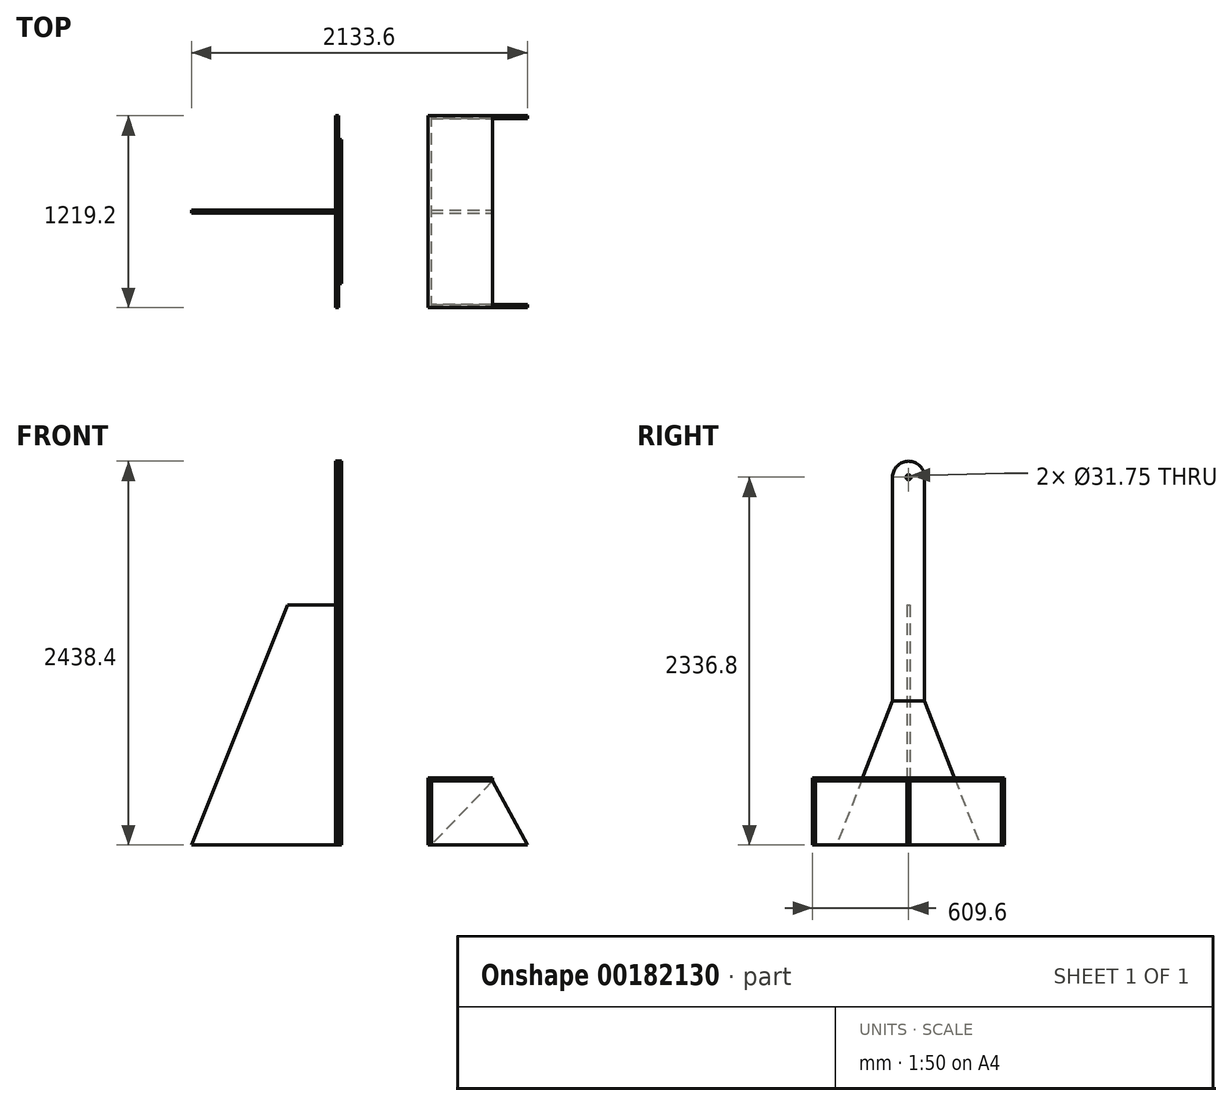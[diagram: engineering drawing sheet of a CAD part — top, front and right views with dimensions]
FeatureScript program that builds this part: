
annotation { "Feature Type Name" : "Feature", "Feature Type Description" : "" }
export const myFeature = defineFeature(function(context is Context, id is Id, definition is map)
    precondition{}
    {
        {
            var Q0;
            Q0=qCreatedBy(makeId("Right.planeOp"),FACE);
            var sketch = newSketch(context, id + "F0", { "sketchPlane" : qUnion([Q0])});
            skLineSegment(sketch, "E0", {"start": v(0, 0) * mm, "end": v(0, 2438.4) * mm, "construction": true});
            skLineSegment(sketch, "E1", {"start": v(-609.6, 0) * mm, "end": v(609.6, 0) * mm, "construction": true});
            skArc(sketch, "E2", {"start": v(101.6, 2336.8) * mm, "mid": v(0, 2438.4) * mm, "end": v(-101.6, 2336.8) * mm});
            skLineSegment(sketch, "E3", {"start": v(-101.6, 2336.8) * mm, "end": v(-101.6, 406.4) * mm});
            skLineSegment(sketch, "E4", {"start": v(101.6, 2336.8) * mm, "end": v(101.6, 406.4) * mm});
            skLineSegment(sketch, "E5", {"start": v(-609.6, 0) * mm, "end": v(-609.6, 406.4) * mm, "construction": true});
            skLineSegment(sketch, "E6", {"start": v(-609.6, 406.4) * mm, "end": v(-101.6, 406.4) * mm, "construction": true});
            skLineSegment(sketch, "E7", {"start": v(101.6, 2336.8) * mm, "end": v(-101.6, 2336.8) * mm, "construction": true});
            skLineSegment(sketch, "E8.MirrorCS", {"start": v(609.6, 406.4) * mm, "end": v(101.6, 406.4) * mm, "construction": true});
            skLineSegment(sketch, "E9.MirrorCS", {"start": v(609.6, 0) * mm, "end": v(609.6, 406.4) * mm, "construction": true});
            skLineSegment(sketch, "E10", {"start": v(-101.6, 406.4) * mm, "end": v(101.6, 406.4) * mm});
            skSolve(sketch);
        }
        {
            var Q0;
            Q0 = qSketchRegion(id + "F0", true);
            var Q1;
            Q1 = qConstructionFilter(qBodyType(qCreatedBy(id + "F0" ,EDGE), BodyType.WIRE), ConstructionObject.NO);
            extrude(context, id + "F1", {"entities" : qUnion([Q0]), "surfaceEntities" : qUnion([Q1]), "depth" : 19.05 * mm});
        }
        {
            var Q0;
            Q0=qCreatedBy(makeId("Right.planeOp"),FACE);
            var sketch = newSketch(context, id + "F2", { "sketchPlane" : qUnion([Q0])});
            skLineSegment(sketch, "E11.0", {"start": v(-609.6, 0) * mm, "end": v(-609.6, 406.4) * mm});
            skLineSegment(sketch, "E12.0", {"start": v(-609.6, 0) * mm, "end": v(609.6, 0) * mm});
            skLineSegment(sketch, "E13.0", {"start": v(609.6, 0) * mm, "end": v(609.6, 406.4) * mm});
            skLineSegment(sketch, "E14", {"start": v(-609.6, 406.4) * mm, "end": v(609.6, 406.4) * mm});
            skSolve(sketch);
        }
        {
            var Q0;
            Q0 = qSketchRegion(id + "F2", true);
            var Q1;
            Q1=makeQuery(id+"F1.opExtrude","CAP_FACE",FACE,{"disambiguationData":[OSD([sQuery(id+"F0.wireOp",EDGE,"E2"),sQuery(id+"F0.wireOp",EDGE,"E3"),sQuery(id+"F0.wireOp",EDGE,"E4"),sQuery(id+"F0.wireOp",EDGE,"E10")])],"isStart":false});
            extrude(context, id + "F3", {"entities" : qUnion([Q0]), "endBound" : BoundingType.UP_TO_SURFACE, "endBoundEntityFace" : qUnion([Q1]), "depth" : 25.4 * mm});
        }
        {
            var Q0;
            Q0=qCreatedBy(makeId("Right.planeOp"),FACE);
            cPlane(context, id + "F4", {"entities" : qUnion([Q0]), "cplaneType" : CPlaneType.OFFSET, "offset" : 304.8 * mm, "width" : 152.4 * mm, "height" : 152.4 * mm});
        }
        {
            var Q0;
            Q0=makeQuery(id+"F3.opExtrude","SWEPT_BODY",BODY,{"disambiguationData":[OSD([sQuery(id+"F2.wireOp",EDGE,"E11.0"),sQuery(id+"F2.wireOp",EDGE,"E12.0"),sQuery(id+"F2.wireOp",EDGE,"E13.0"),sQuery(id+"F2.wireOp",EDGE,"E14")])]});
            var Q1;
            Q1=qCreatedBy(id+"F4.planeOp",FACE);
            mirror(context, id + "F5", {"entities" : qUnion([Q0]), "mirrorPlane" : qUnion([Q1])});
        }
        {
            var Q0;
            Q0=makeQuery(id+"F1.opExtrude","CAP_FACE",FACE,{"disambiguationData":[OSD([sQuery(id+"F0.wireOp",EDGE,"E2"),sQuery(id+"F0.wireOp",EDGE,"E3"),sQuery(id+"F0.wireOp",EDGE,"E4"),sQuery(id+"F0.wireOp",EDGE,"E10")])],"isStart":false});
            var sketch = newSketch(context, id + "F6", { "sketchPlane" : qUnion([Q0])});
            skLineSegment(sketch, "E15", {"start": v(-101.6, 914.4) * mm, "end": v(101.6, 914.4) * mm});
            skLineSegment(sketch, "E16", {"start": v(-457.2, 0) * mm, "end": v(457.2, 0) * mm});
            skLineSegment(sketch, "E17", {"start": v(-101.6, 914.4) * mm, "end": v(-457.2, 0) * mm});
            skLineSegment(sketch, "E18", {"start": v(101.6, 914.4) * mm, "end": v(457.2, 0) * mm});
            skSolve(sketch);
        }
        {
            var Q0;
            Q0 = qSketchRegion(id + "F6", true);
            extrude(context, id + "F7", {"entities" : qUnion([Q0]), "depth" : 19.05 * mm});
        }
        {
            var Q0;
            Q0=makeQuery(id+"F5.opPattern","COPY",FACE,{"derivedFrom":makeQuery(id+"F3.opExtrude","SWEPT_FACE",FACE,{"disambiguationData":[OSD([sQuery(id+"F2.wireOp",EDGE,"E14")])]}),"instanceName":"1"});
            var sketch = newSketch(context, id + "F8", { "sketchPlane" : qUnion([Q0])});
            skLineSegment(sketch, "E19.bottom", {"start": v(590.55, -609.6) * mm, "end": v(996.95, -609.6) * mm});
            skLineSegment(sketch, "E19.top", {"start": v(590.55, 609.6) * mm, "end": v(996.95, 609.6) * mm});
            skLineSegment(sketch, "E19.left", {"start": v(590.55, -609.6) * mm, "end": v(590.55, 609.6) * mm});
            skLineSegment(sketch, "E19.right", {"start": v(996.95, -609.6) * mm, "end": v(996.95, 609.6) * mm});
            skSolve(sketch);
        }
        {
            var Q0;
            Q0 = qSketchRegion(id + "F8", true);
            extrude(context, id + "F9", {"entities" : qUnion([Q0]), "depth" : 19.05 * mm});
        }
        {
            var Q0;
            Q0=makeQuery(id+"F9.opExtrude","SWEPT_FACE",FACE,{"disambiguationData":[OSD([sQuery(id+"F8.wireOp",EDGE,"E19.bottom")])]});
            var sketch = newSketch(context, id + "F10", { "sketchPlane" : qUnion([Q0])});
            skLineSegment(sketch, "E20.0", {"start": v(609.6, 406.4) * mm, "end": v(996.95, 406.4) * mm});
            skLineSegment(sketch, "E21.0", {"start": v(609.6, 0) * mm, "end": v(609.6, 406.4) * mm});
            skPoint(sketch, "E22.orphan", {"position": v(590.55, 406.4) * mm});
            skLineSegment(sketch, "E23", {"start": v(996.95, 406.4) * mm, "end": v(1219.2, 0) * mm});
            skLineSegment(sketch, "E24", {"start": v(1219.2, 0) * mm, "end": v(609.6, 0) * mm});
            skSolve(sketch);
        }
        {
            var Q0;
            Q0 = qSketchRegion(id + "F10", true);
            extrude(context, id + "F11", {"entities" : qUnion([Q0]), "oppositeDirection" : true, "depth" : 19.05 * mm});
        }
        {
            var Q0;
            Q0=makeQuery(id+"F11.opExtrude","SWEPT_BODY",BODY,{"disambiguationData":[OSD([sQuery(id+"F10.wireOp",EDGE,"E20.0"),sQuery(id+"F10.wireOp",EDGE,"E21.0"),sQuery(id+"F10.wireOp",EDGE,"E23"),sQuery(id+"F10.wireOp",EDGE,"E24")])]});
            var Q1;
            Q1=qCreatedBy(makeId("Front.planeOp"),FACE);
            mirror(context, id + "F12", {"entities" : qUnion([Q0]), "mirrorPlane" : qUnion([Q1])});
        }
        {
            var Q0;
            Q0=qCreatedBy(makeId("Front.planeOp"),FACE);
            var sketch = newSketch(context, id + "F13", { "sketchPlane" : qUnion([Q0])});
            skLineSegment(sketch, "E25.0", {"start": v(609.6, 406.4) * mm, "end": v(996.95, 406.4) * mm});
            skLineSegment(sketch, "E26.0", {"start": v(609.6, 0) * mm, "end": v(609.6, 406.4) * mm});
            skPoint(sketch, "E27.orphan", {"position": v(590.55, 406.4) * mm});
            skLineSegment(sketch, "E28", {"start": v(996.95, 406.4) * mm, "end": v(609.6, 0) * mm});
            skSolve(sketch);
        }
        {
            var Q0;
            Q0 = qSketchRegion(id + "F13", true);
            extrude(context, id + "F14", {"entities" : qUnion([Q0]), "endBound" : BoundingType.SYMMETRIC, "depth" : 19.05 * mm});
        }
        {
            var Q0;
            Q0=qCreatedBy(makeId("Front.planeOp"),FACE);
            var sketch = newSketch(context, id + "F15", { "sketchPlane" : qUnion([Q0])});
            skLineSegment(sketch, "E29.0", {"start": v(0, 2336.8) * mm, "end": v(0, 406.4) * mm});
            skLineSegment(sketch, "E30", {"start": v(-304.8, 1524) * mm, "end": v(-914.4, 0) * mm});
            skLineSegment(sketch, "E31", {"start": v(-914.4, 0) * mm, "end": v(0, 0) * mm});
            skLineSegment(sketch, "E32.0", {"start": v(0, 0) * mm, "end": v(0, 406.4) * mm});
            skLineSegment(sketch, "E33", {"start": v(0, 1524) * mm, "end": v(-304.8, 1524) * mm});
            skSolve(sketch);
        }
        {
            var Q0;
            Q0 = qSketchRegion(id + "F15", true);
            extrude(context, id + "F16", {"entities" : qUnion([Q0]), "endBound" : BoundingType.SYMMETRIC, "depth" : 19.05 * mm});
        }
        {
            var Q0;
            Q0=makeQuery(id+"F1.opExtrude","CAP_FACE",FACE,{"disambiguationData":[OSD([sQuery(id+"F0.wireOp",EDGE,"E2"),sQuery(id+"F0.wireOp",EDGE,"E3"),sQuery(id+"F0.wireOp",EDGE,"E4"),sQuery(id+"F0.wireOp",EDGE,"E10")])],"isStart":false});
            var sketch = newSketch(context, id + "F17", { "sketchPlane" : qUnion([Q0])});
            skArc(sketch, "E34.0", {"start": v(101.6, 2336.8) * mm, "mid": v(0, 2438.4) * mm, "end": v(-101.6, 2336.8) * mm});
            skLineSegment(sketch, "E35.0", {"start": v(-101.6, 2336.8) * mm, "end": v(-101.6, 914.4) * mm});
            skLineSegment(sketch, "E36.0", {"start": v(101.6, 2336.8) * mm, "end": v(101.6, 914.4) * mm});
            skLineSegment(sketch, "E37.0", {"start": v(-101.6, 914.4) * mm, "end": v(101.6, 914.4) * mm});
            skPoint(sketch, "E38.orphan", {"position": v(-101.6, 406.4) * mm});
            skPoint(sketch, "E39.orphan", {"position": v(101.6, 406.4) * mm});
            skSolve(sketch);
        }
        {
            var Q0;
            Q0 = qSketchRegion(id + "F17", true);
            var Q1;
            Q1=makeQuery(id+"F7.opExtrude","CAP_FACE",FACE,{"disambiguationData":[OSD([sQuery(id+"F6.wireOp",EDGE,"E15"),sQuery(id+"F6.wireOp",EDGE,"E16"),sQuery(id+"F6.wireOp",EDGE,"E17"),sQuery(id+"F6.wireOp",EDGE,"E18")])],"isStart":false});
            extrude(context, id + "F18", {"entities" : qUnion([Q0]), "endBound" : BoundingType.UP_TO_SURFACE, "endBoundEntityFace" : qUnion([Q1]), "depth" : 25.4 * mm});
        }
        {
            var Q0;
            Q0=makeQuery(id+"F0.imprint","IMPRINT",FACE,{"disambiguationData":[TD([[makeQuery(id+"F0.imprint","IMPRINT",EDGE,{"derivedFrom":sQuery(id+"F0.wireOp",EDGE,"E2")}),1.0]])]});
            var sketch = newSketch(context, id + "F19", { "sketchPlane" : qUnion([Q0])});
            skCircle(sketch, "E40", {"center": v(0, 2336.8) * mm, "radius": 15.88 * mm});
            skSolve(sketch);
        }
        {
            var Q0;
            Q0 = qSketchRegion(id + "F19", true);
            extrude(context, id + "F20", {"entities" : qUnion([Q0]), "operationType" : NewBodyOperationType.REMOVE, "endBound" : BoundingType.THROUGH_ALL, "depth" : 25.4 * mm});
        }
    });
